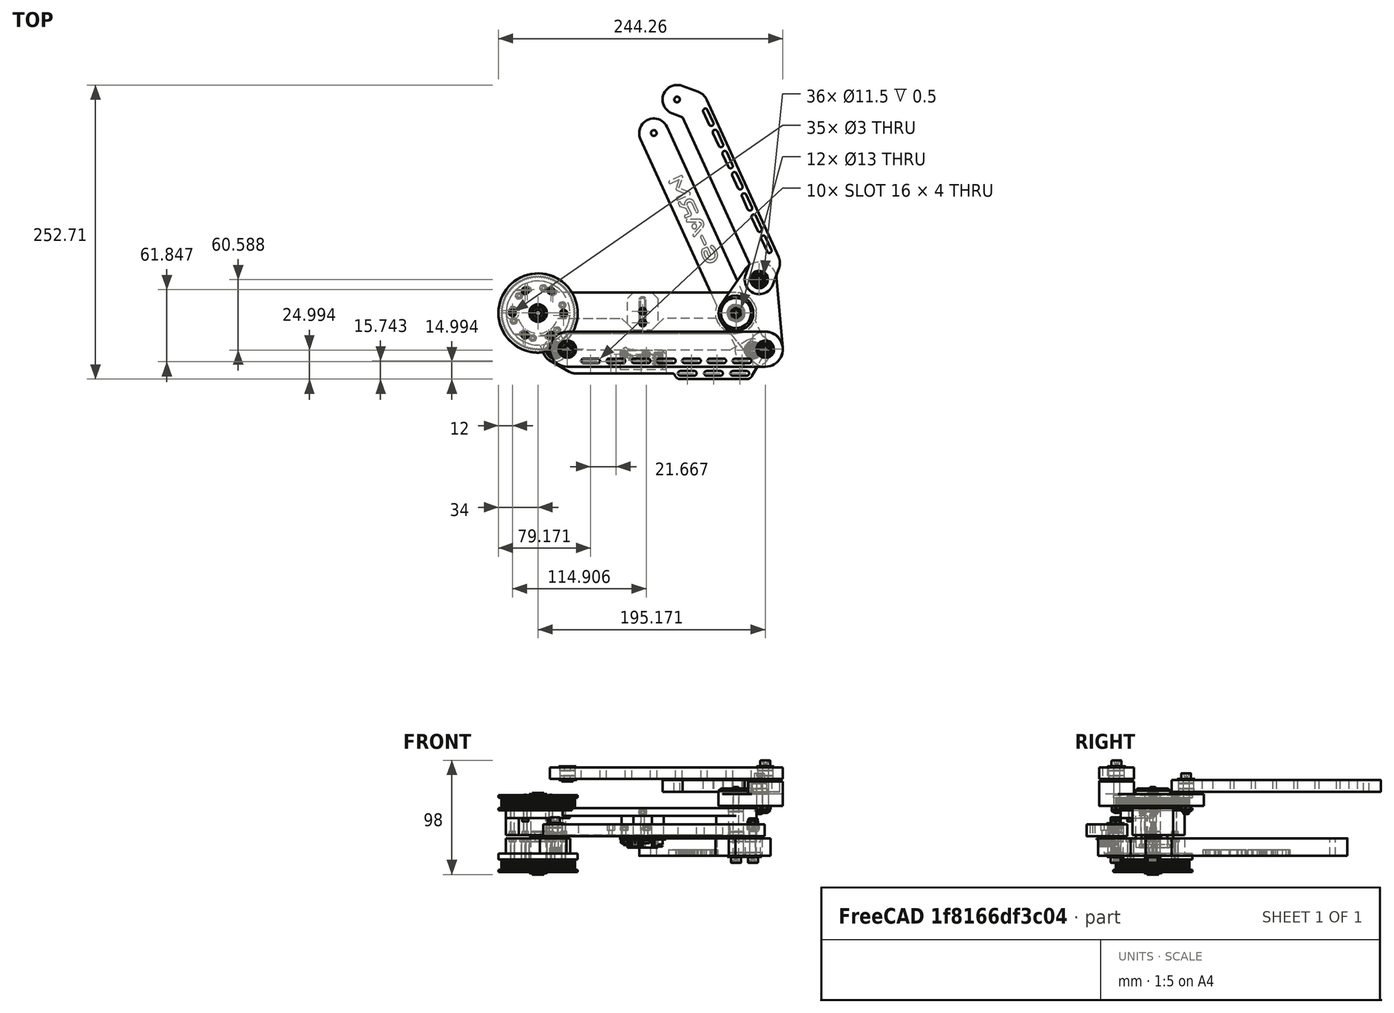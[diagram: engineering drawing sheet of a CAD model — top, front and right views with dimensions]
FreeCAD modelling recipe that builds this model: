
FCSTD DOCUMENT  (FreeCAD 0.20R29410 (Git))
Label: #0_ASSEMBLY_LINKS
License: All rights reserved
LicenseURL: http://en.wikipedia.org/wiki/All_rights_reserved
objects: Part::FeaturePython×105, App::FeaturePython×86
note: 105 computed .brp shape members not serialized (recipe doc carries the construction recipe); baked Part::Feature solids carry a one-line shape summary decoded from their .brp

FEATURE [Part::FeaturePython] b__11_Link1_001_  label="#11_Link1_001"  # a2plus imported part (geometry in sourceFile) (typed FeaturePython)
  a2p_Version = 0.4.60k
  fixedPosition = true
  objectType = a2pPart
  sourceFile = .\#11_Link1.FCStd
  subassemblyImport = false
  timeLastImport = 1.68867e+09
  updateColors = true
FEATURE [Part::FeaturePython] b_F6951_001_  label="F6951_001"  # a2plus imported part (geometry in sourceFile) (typed FeaturePython)
  Placement = pos=(-2.35677e-08,2.78792e-08,3) rot=(0.871292,0.490765,0;3.14159rad)
  a2p_Version = 0.4.60k
  fixedPosition = false
  objectType = a2pPart
  sourceFile = .\..\Complements\F695.step
  subassemblyImport = false
  timeLastImport = 1.6885e+09
  updateColors = true
FEATURE [Part::FeaturePython] b_F6951_001_001  label="F6951_002"  # a2plus imported part (geometry in sourceFile) (typed FeaturePython)
  Placement = pos=(170,-3.90484e-08,3) rot=(-0.661453,0.749987,0;3.14159rad)
  a2p_Version = 0.4.60k
  fixedPosition = false
  objectType = a2pPart
  sourceFile = .\..\Complements\F695.step
  subassemblyImport = false
  timeLastImport = 1.6885e+09
  updateColors = true
FEATURE [Part::FeaturePython] b_F6951_001_002  label="F6951_003"  # a2plus imported part (geometry in sourceFile) (typed FeaturePython)
  Placement = pos=(170,-4.90656e-08,20) rot=(-2e-06,0,1;0.008933rad)
  a2p_Version = 0.4.60k
  fixedPosition = false
  objectType = a2pPart
  sourceFile = .\..\Complements\F695.step
  subassemblyImport = false
  timeLastImport = 1.6885e+09
  updateColors = true
FEATURE [Part::FeaturePython] b_F6951_001_003  label="F6951_004"  # a2plus imported part (geometry in sourceFile) (typed FeaturePython)
  Placement = pos=(170,8.08089e-07,-6) rot=(1.8e-05,1.3e-05,-1;0.009624rad)
  a2p_Version = 0.4.60k
  fixedPosition = false
  objectType = a2pPart
  sourceFile = .\..\Complements\F695.step
  subassemblyImport = false
  timeLastImport = 1.6885e+09
  updateColors = true
FEATURE [Part::FeaturePython] b_F6951_001_005  label="F6951_006"  # a2plus imported part (geometry in sourceFile) (typed FeaturePython)
  Placement = pos=(0,1.12014e-07,31) rot=(0,0,1;0rad)
  a2p_Version = 0.4.60k
  fixedPosition = false
  objectType = a2pPart
  sourceFile = .\..\Complements\F695.step
  subassemblyImport = false
  timeLastImport = 1.6885e+09
  updateColors = true
FEATURE [Part::FeaturePython] b_F6951_001_006  label="F6951_007"  # a2plus imported part (geometry in sourceFile) (typed FeaturePython)
  Placement = pos=(184.542,-31.8361,-6.00001) rot=(0.000409,0.000277,1;0.00082rad)
  a2p_Version = 0.4.60k
  fixedPosition = false
  objectType = a2pPart
  sourceFile = .\..\Complements\F695.step
  subassemblyImport = false
  timeLastImport = 1.6885e+09
  updateColors = true
FEATURE [Part::FeaturePython] b_F6951_001_007  label="F6951_008"  # a2plus imported part (geometry in sourceFile) (typed FeaturePython)
  Placement = pos=(170,3.90411e-06,-15) rot=(-0.543177,0.839618,0;3.14159rad)
  a2p_Version = 0.4.60k
  fixedPosition = false
  objectType = a2pPart
  sourceFile = .\..\Complements\F695.step
  subassemblyImport = false
  timeLastImport = 1.6885e+09
  updateColors = true
FEATURE [Part::FeaturePython] b_F6951_001_008  label="F6951_009"  # a2plus imported part (geometry in sourceFile) (typed FeaturePython)
  Placement = pos=(1.64685e-07,-6.27281e-08,-6) rot=(0,-1e-06,-1;0.041178rad)
  a2p_Version = 0.4.60k
  fixedPosition = false
  objectType = a2pPart
  sourceFile = .\..\Complements\F695.step
  subassemblyImport = false
  timeLastImport = 1.6885e+09
  updateColors = true
FEATURE [Part::FeaturePython] b_F6951_001_009  label="F6951_010"  # a2plus imported part (geometry in sourceFile) (typed FeaturePython)
  Placement = pos=(184.542,-31.8361,-15) rot=(0.590696,0.806894,0;3.14159rad)
  a2p_Version = 0.4.60k
  fixedPosition = false
  objectType = a2pPart
  sourceFile = .\..\Complements\F695.step
  subassemblyImport = false
  timeLastImport = 1.6885e+09
  updateColors = true
FEATURE [App::FeaturePython] circularEdge_001  label="circularEdge_001__#11_Link1_001"  # a2plus constraint (typed FeaturePython)
  Object1 = b_F6951_001_
  Object2 = b__11_Link1_001_
  ParentTreeObject = -> b_F6951_001_
  SubElement1 = Edge18
  SubElement2 = Edge14
  Suppressed = false
  Type = circularEdge
  directionConstraint = 1
  lockRotation = false
  offset = 0
FEATURE [App::FeaturePython] circularEdge_001_mirror  label="circularEdge_001__F6951_001"  # a2plus constraint (typed FeaturePython)
  Object1 = b_F6951_001_
  Object2 = b__11_Link1_001_
  ParentTreeObject = -> b__11_Link1_001_
  SubElement1 = Edge18
  SubElement2 = Edge14
  Suppressed = false
  Type = circularEdge
  directionConstraint = 1
  lockRotation = false
  offset = 0
FEATURE [App::FeaturePython] circularEdge_002  label="circularEdge_002__#11_Link1_001"  # a2plus constraint (typed FeaturePython)
  Object1 = b_F6951_001_001
  Object2 = b__11_Link1_001_
  ParentTreeObject = -> b_F6951_001_001
  SubElement1 = Edge18
  SubElement2 = Edge18
  Suppressed = false
  Type = circularEdge
  directionConstraint = 1
  lockRotation = false
  offset = 0
FEATURE [App::FeaturePython] circularEdge_002_mirror  label="circularEdge_002__F6951_002"  # a2plus constraint (typed FeaturePython)
  Object1 = b_F6951_001_001
  Object2 = b__11_Link1_001_
  ParentTreeObject = -> b__11_Link1_001_
  SubElement1 = Edge18
  SubElement2 = Edge18
  Suppressed = false
  Type = circularEdge
  directionConstraint = 1
  lockRotation = false
  offset = 0
FEATURE [App::FeaturePython] circularEdge_003  label="circularEdge_003__#11_Link1_001"  # a2plus constraint (typed FeaturePython)
  Object1 = b_F6951_001_002
  Object2 = b__11_Link1_001_
  ParentTreeObject = -> b_F6951_001_002
  SubElement1 = Edge18
  SubElement2 = Edge62
  Suppressed = false
  Type = circularEdge
  directionConstraint = 0
  lockRotation = false
  offset = 0
FEATURE [App::FeaturePython] circularEdge_003_mirror  label="circularEdge_003__F6951_003"  # a2plus constraint (typed FeaturePython)
  Object1 = b_F6951_001_002
  Object2 = b__11_Link1_001_
  ParentTreeObject = -> b__11_Link1_001_
  SubElement1 = Edge18
  SubElement2 = Edge62
  Suppressed = false
  Type = circularEdge
  directionConstraint = 0
  lockRotation = false
  offset = 0
FEATURE [Part::FeaturePython] b__10_MotorsBasePulleys_001_  label="#10_MotorsBasePulleys_001"  # a2plus imported part (geometry in sourceFile) (typed FeaturePython)
  Placement = pos=(-11.651,-43.4819,23) rot=(0,0,1;0.523599rad)
  a2p_Version = 0.4.60k
  fixedPosition = false
  objectType = a2pPart
  sourceFile = .\#10_MotorsBasePulleys.FCStd
  subassemblyImport = false
  timeLastImport = 1.68295e+09
  updateColors = true
FEATURE [App::FeaturePython] circularEdge_004  label="circularEdge_004__#11_Link1_001"  # a2plus constraint (typed FeaturePython)
  Object1 = b__10_MotorsBasePulleys_001_
  Object2 = b__11_Link1_001_
  ParentTreeObject = -> b__10_MotorsBasePulleys_001_
  SubElement1 = Edge2166
  SubElement2 = Edge47
  Suppressed = false
  Type = circularEdge
  directionConstraint = 0
  lockRotation = false
  offset = 0
FEATURE [App::FeaturePython] circularEdge_004_mirror  label="circularEdge_004__#10_MotorsBasePulleys_001"  # a2plus constraint (typed FeaturePython)
  Object1 = b__10_MotorsBasePulleys_001_
  Object2 = b__11_Link1_001_
  ParentTreeObject = -> b__11_Link1_001_
  SubElement1 = Edge2166
  SubElement2 = Edge47
  Suppressed = false
  Type = circularEdge
  directionConstraint = 0
  lockRotation = false
  offset = 0
FEATURE [App::FeaturePython] circularEdge_005  label="circularEdge_005__#10_MotorsBasePulleys_001"  # a2plus constraint (typed FeaturePython)
  Object1 = b_F6951_001_005
  Object2 = b__10_MotorsBasePulleys_001_
  ParentTreeObject = -> b_F6951_001_005
  SubElement1 = Edge18
  SubElement2 = Edge716
  Suppressed = false
  Type = circularEdge
  directionConstraint = 0
  lockRotation = false
  offset = 0
FEATURE [App::FeaturePython] circularEdge_005_mirror  label="circularEdge_005__F6951_006"  # a2plus constraint (typed FeaturePython)
  Object1 = b_F6951_001_005
  Object2 = b__10_MotorsBasePulleys_001_
  ParentTreeObject = -> b__10_MotorsBasePulleys_001_
  SubElement1 = Edge18
  SubElement2 = Edge716
  Suppressed = false
  Type = circularEdge
  directionConstraint = 0
  lockRotation = false
  offset = 0
FEATURE [Part::FeaturePython] Screw  label="M3x30-Tornillo"  # Fasteners workbench fastener (typed FeaturePython)
  Placement = pos=(-22,0,3) rot=(1,0,0;3.14159rad)
  baseObject = -> b__11_Link1_001_ [Edge85]
  diameter = 4
  invert = false
  leftHanded = false
  length = 10
  lengthCustom = 30
  matchOuter = false
  offset = 0
  thread = false
  type = 45
FEATURE [Part::FeaturePython] Screw001  label="M3x30-Tornillo001"  # Fasteners workbench fastener (typed FeaturePython)
  Placement = pos=(22,-3e-15,3) rot=(1,0,0;3.14159rad)
  baseObject = -> b__11_Link1_001_ [Edge87]
  diameter = 4
  invert = false
  leftHanded = false
  length = 10
  lengthCustom = 30
  matchOuter = false
  offset = 0
  thread = false
  type = 45
FEATURE [Part::FeaturePython] Screw002  label="M3x30-Tornillo002"  # Fasteners workbench fastener (typed FeaturePython)
  Placement = pos=(11,19.0526,3) rot=(1,0,0;3.14159rad)
  baseObject = -> b__11_Link1_001_ [Edge103]
  diameter = 4
  invert = false
  leftHanded = false
  length = 10
  lengthCustom = 30
  matchOuter = false
  offset = 0
  thread = false
  type = 45
FEATURE [Part::FeaturePython] Screw003  label="M3x30-Tornillo003"  # Fasteners workbench fastener (typed FeaturePython)
  Placement = pos=(-11,19.0526,3) rot=(1,0,0;3.14159rad)
  baseObject = -> b__11_Link1_001_ [Edge101]
  diameter = 4
  invert = false
  leftHanded = false
  length = 10
  lengthCustom = 30
  matchOuter = false
  offset = 0
  thread = false
  type = 45
FEATURE [App::FeaturePython] circularEdge_006  label="circularEdge_006__#11_Link1_001"  # a2plus constraint (typed FeaturePython)
  Object1 = b__10_MotorsBasePulleys_001_
  Object2 = b__11_Link1_001_
  ParentTreeObject = -> b__10_MotorsBasePulleys_001_
  SubElement1 = Edge2217
  SubElement2 = Edge55
  Suppressed = false
  Type = circularEdge
  directionConstraint = 1
  lockRotation = false
  offset = 0
FEATURE [App::FeaturePython] circularEdge_006_mirror  label="circularEdge_006__#10_MotorsBasePulleys_001"  # a2plus constraint (typed FeaturePython)
  Object1 = b__10_MotorsBasePulleys_001_
  Object2 = b__11_Link1_001_
  ParentTreeObject = -> b__11_Link1_001_
  SubElement1 = Edge2217
  SubElement2 = Edge55
  Suppressed = false
  Type = circularEdge
  directionConstraint = 1
  lockRotation = false
  offset = 0
FEATURE [Part::FeaturePython] Screw004  label="M3x20-Tornillo"  # Fasteners workbench fastener (typed FeaturePython)
  Placement = pos=(-11,-19.0526,14.5) rot=(1,0,0;3.14159rad)
  baseObject = -> b__11_Link1_001_ [Edge123]
  diameter = 4
  invert = false
  leftHanded = false
  length = 10
  lengthCustom = 20
  matchOuter = false
  offset = 0
  thread = false
  type = 45
FEATURE [Part::FeaturePython] Screw005  label="M3x20-Tornillo001"  # Fasteners workbench fastener (typed FeaturePython)
  Placement = pos=(11,-19.0526,14.5) rot=(1,0,0;3.14159rad)
  baseObject = -> b__11_Link1_001_ [Edge121]
  diameter = 4
  invert = false
  leftHanded = false
  length = 10
  lengthCustom = 20
  matchOuter = false
  offset = 0
  thread = false
  type = 45
FEATURE [Part::FeaturePython] Nut  label="M3-Tuerca"  # Fasteners workbench fastener (typed FeaturePython)
  Placement = pos=(-22,7.42124e-07,29) rot=(0,0,1;0rad)
  baseObject = -> b__10_MotorsBasePulleys_001_ [Edge2224]
  diameter = 1
  invert = false
  leftHanded = false
  matchOuter = false
  offset = 0
  thread = false
  type = 19
FEATURE [Part::FeaturePython] Nut001  label="M3-Tuerca001"  # Fasteners workbench fastener (typed FeaturePython)
  Placement = pos=(-11,19.0526,29) rot=(0,0,1;0rad)
  baseObject = -> b__10_MotorsBasePulleys_001_ [Edge2226]
  diameter = 1
  invert = false
  leftHanded = false
  matchOuter = false
  offset = 0
  thread = false
  type = 19
FEATURE [Part::FeaturePython] Nut002  label="M3-Tuerca002"  # Fasteners workbench fastener (typed FeaturePython)
  Placement = pos=(11,19.0526,29) rot=(0,0,1;0rad)
  baseObject = -> b__10_MotorsBasePulleys_001_ [Edge2225]
  diameter = 1
  invert = false
  leftHanded = false
  matchOuter = false
  offset = 0
  thread = false
  type = 19
FEATURE [Part::FeaturePython] Nut003  label="M3-Tuerca003"  # Fasteners workbench fastener (typed FeaturePython)
  Placement = pos=(-11,-19.0526,29) rot=(0,0,1;0rad)
  baseObject = -> b__10_MotorsBasePulleys_001_ [Edge2222]
  diameter = 1
  invert = false
  leftHanded = false
  matchOuter = false
  offset = 0
  thread = false
  type = 19
FEATURE [Part::FeaturePython] Nut004  label="M3-Tuerca004"  # Fasteners workbench fastener (typed FeaturePython)
  Placement = pos=(22,-2.47375e-07,29) rot=(0,0,1;0rad)
  baseObject = -> b__10_MotorsBasePulleys_001_ [Edge2223]
  diameter = 1
  invert = false
  leftHanded = false
  matchOuter = false
  offset = 0
  thread = false
  type = 19
FEATURE [Part::FeaturePython] Nut005  label="M3-Tuerca005"  # Fasteners workbench fastener (typed FeaturePython)
  Placement = pos=(11,-19.0526,29) rot=(0,0,1;0rad)
  baseObject = -> b__10_MotorsBasePulleys_001_ [Edge2221]
  diameter = 1
  invert = false
  leftHanded = false
  matchOuter = false
  offset = 0
  thread = false
  type = 19
FEATURE [Part::FeaturePython] Nut006  label="M3-Tuerca008"  # Fasteners workbench fastener (typed FeaturePython)
  Placement = pos=(89.762,1.5,18) rot=(0,0,1;0rad)
  baseObject = -> b__11_Link1_001_ [Edge79]
  diameter = 1
  invert = true
  leftHanded = false
  matchOuter = false
  offset = 0
  thread = false
  type = 19
FEATURE [Part::FeaturePython] Nut007  label="M3-Tuerca009"  # Fasteners workbench fastener (typed FeaturePython)
  Placement = pos=(89.762,-8.5,18) rot=(0,0,1;0rad)
  baseObject = -> b__11_Link1_001_ [Edge77]
  diameter = 1
  invert = true
  leftHanded = false
  matchOuter = false
  offset = 0
  thread = false
  type = 19
FEATURE [Part::FeaturePython] b__18_EndStopLink2Adjust_001_  label="#18_EndStopLink2Adjust_001"  # a2plus imported part (geometry in sourceFile) (typed FeaturePython)
  Placement = pos=(89.762,1.5,-9.71845e-08) rot=(-0.707107,0.707107,0;3.14159rad)
  a2p_Version = 0.4.60k
  fixedPosition = false
  objectType = a2pPart
  sourceFile = .\#18_EndStopLink2Adjust.FCStd
  subassemblyImport = false
  timeLastImport = 1.68302e+09
  updateColors = true
FEATURE [App::FeaturePython] angledPlanes_001  label="angledPlanes_001__#11_Link1_001"  # a2plus constraint (typed FeaturePython)
  Object1 = b__18_EndStopLink2Adjust_001_
  Object2 = b__11_Link1_001_
  ParentTreeObject = -> b__18_EndStopLink2Adjust_001_
  SubElement1 = Face14
  SubElement2 = Face9
  Suppressed = false
  Type = angledPlanes
  angle = 90
FEATURE [App::FeaturePython] angledPlanes_001_mirror  label="angledPlanes_001__#18_EndStopLink2Adjust_001"  # a2plus constraint (typed FeaturePython)
  Object1 = b__18_EndStopLink2Adjust_001_
  Object2 = b__11_Link1_001_
  ParentTreeObject = -> b__11_Link1_001_
  SubElement1 = Face14
  SubElement2 = Face9
  Suppressed = false
  Type = angledPlanes
  angle = 90
FEATURE [Part::FeaturePython] Screw006  label="M3x30-Tornillo006"  # Fasteners workbench fastener (typed FeaturePython)
  Placement = pos=(89.762,-8.5,-8) rot=(1,0,0;3.14159rad)
  baseObject = -> b__11_Link1_001_ [Edge16]
  diameter = 4
  invert = false
  leftHanded = false
  length = 10
  lengthCustom = 30
  matchOuter = false
  offset = 8
  thread = false
  type = 45
FEATURE [Part::FeaturePython] Screw007  label="M3x30-Tornillo005"  # Fasteners workbench fastener (typed FeaturePython)
  Placement = pos=(89.762,1.5,-8) rot=(1,0,0;3.14159rad)
  baseObject = -> b__11_Link1_001_ [Edge17]
  diameter = 4
  invert = false
  leftHanded = false
  length = 10
  lengthCustom = 30
  matchOuter = false
  offset = 8
  thread = false
  type = 45
FEATURE [Part::FeaturePython] Washer  label="M5-Arandela"  # Fasteners workbench fastener (typed FeaturePython)
  Placement = pos=(-7.78767e-09,1.38263e-08,-1) rot=(0.871295,0.490759,0;3.14159rad)
  baseObject = -> b_F6951_001_ [Edge17]
  diameter = 6
  invert = true
  matchOuter = false
  offset = 0
  type = 4
FEATURE [Part::FeaturePython] M5_Arandela_001  label="M5-Arandela_001"  # a2plus imported part (geometry in sourceFile) (typed FeaturePython)
  Placement = pos=(3.60617e-08,-3.8045e-08,-3) rot=(0.871295,0.490759,0;3.14159rad)
  a2p_Version = 0.4.60k
  fixedPosition = false
  localSourceObject = Washer
  objectType = a2pPart
  sourceFile = converted
  subassemblyImport = false
  timeLastImport = 1.689e+09
  updateColors = true
FEATURE [App::FeaturePython] circularEdge_008  label="circularEdge_008__F6951_001"  # a2plus constraint (typed FeaturePython)
  Object1 = M5_Arandela_001
  Object2 = b_F6951_001_
  ParentTreeObject = -> M5_Arandela_001
  SubElement1 = Edge2
  SubElement2 = Edge8
  Suppressed = false
  Type = circularEdge
  directionConstraint = 1
  lockRotation = false
  offset = 0
FEATURE [App::FeaturePython] circularEdge_008_mirror  label="circularEdge_008__M5-Arandela_001"  # a2plus constraint (typed FeaturePython)
  Object1 = M5_Arandela_001
  Object2 = b_F6951_001_
  ParentTreeObject = -> b_F6951_001_
  SubElement1 = Edge2
  SubElement2 = Edge8
  Suppressed = false
  Type = circularEdge
  directionConstraint = 1
  lockRotation = false
  offset = 0
FEATURE [Part::FeaturePython] b_M5_Arandela_001_  label="M5-Arandela_002"  # a2plus imported part (geometry in sourceFile) (typed FeaturePython)
  Placement = pos=(170,1.78434e-07,-3) rot=(0.874462,0.485093,0;3.14159rad)
  a2p_Version = 0.4.60k
  fixedPosition = false
  localSourceObject = Washer
  objectType = a2pPart
  sourceFile = converted
  subassemblyImport = false
  timeLastImport = 1.689e+09
  updateColors = true
FEATURE [Part::FeaturePython] b_M5_Arandela_001_001  label="M5-Arandela_003"  # a2plus imported part (geometry in sourceFile) (typed FeaturePython)
  Placement = pos=(184.542,-31.8361,-3.00001) rot=(0.872092,0.489343,0;3.14159rad)
  a2p_Version = 0.4.60k
  fixedPosition = false
  localSourceObject = Washer
  objectType = a2pPart
  sourceFile = converted
  subassemblyImport = false
  timeLastImport = 1.689e+09
  updateColors = true
FEATURE [Part::FeaturePython] b_M5_Arandela_001_002  label="M5-Arandela_004"  # a2plus imported part (geometry in sourceFile) (typed FeaturePython)
  Placement = pos=(14.5419,-31.8361,-4) rot=(0.876459,0.481477,0;3.14159rad)
  a2p_Version = 0.4.60k
  fixedPosition = false
  localSourceObject = Washer
  objectType = a2pPart
  sourceFile = converted
  subassemblyImport = false
  timeLastImport = 1.689e+09
  updateColors = true
FEATURE [App::FeaturePython] circularEdge_009  label="circularEdge_009__F6951_002"  # a2plus constraint (typed FeaturePython)
  Object1 = b_M5_Arandela_001_
  Object2 = b_F6951_001_001
  ParentTreeObject = -> b_M5_Arandela_001_
  SubElement1 = Edge2
  SubElement2 = Edge14
  Suppressed = false
  Type = circularEdge
  directionConstraint = 1
  lockRotation = false
  offset = 0
FEATURE [App::FeaturePython] circularEdge_009_mirror  label="circularEdge_009__M5-Arandela_002"  # a2plus constraint (typed FeaturePython)
  Object1 = b_M5_Arandela_001_
  Object2 = b_F6951_001_001
  ParentTreeObject = -> b_F6951_001_001
  SubElement1 = Edge2
  SubElement2 = Edge14
  Suppressed = false
  Type = circularEdge
  directionConstraint = 1
  lockRotation = false
  offset = 0
FEATURE [App::FeaturePython] circularEdge_010  label="circularEdge_010__M5-Arandela_002"  # a2plus constraint (typed FeaturePython)
  Object1 = b_F6951_001_003
  Object2 = b_M5_Arandela_001_
  ParentTreeObject = -> b_F6951_001_003
  SubElement1 = Edge14
  SubElement2 = Edge3
  Suppressed = false
  Type = circularEdge
  directionConstraint = 0
  lockRotation = false
  offset = 0
FEATURE [App::FeaturePython] circularEdge_010_mirror  label="circularEdge_010__F6951_004"  # a2plus constraint (typed FeaturePython)
  Object1 = b_F6951_001_003
  Object2 = b_M5_Arandela_001_
  ParentTreeObject = -> b_M5_Arandela_001_
  SubElement1 = Edge14
  SubElement2 = Edge3
  Suppressed = false
  Type = circularEdge
  directionConstraint = 0
  lockRotation = false
  offset = 0
FEATURE [Part::FeaturePython] b__19_Link2_001_  label="#19_Link2_001"  # a2plus imported part (geometry in sourceFile) (typed FeaturePython)
  Placement = pos=(170,2.89051e-07,-3) rot=(0.54061,0.841273,0;3.14159rad)
  a2p_Version = 0.4.60k
  fixedPosition = false
  objectType = a2pPart
  sourceFile = .\#19_Link2.FCStd
  subassemblyImport = false
  timeLastImport = 1.68302e+09
  updateColors = true
FEATURE [App::FeaturePython] circularEdge_011  label="circularEdge_011__F6951_004"  # a2plus constraint (typed FeaturePython)
  Object1 = b__19_Link2_001_
  Object2 = b_F6951_001_003
  ParentTreeObject = -> b__19_Link2_001_
  SubElement1 = Edge17
  SubElement2 = Edge18
  Suppressed = false
  Type = circularEdge
  directionConstraint = 1
  lockRotation = false
  offset = 0
FEATURE [App::FeaturePython] circularEdge_011_mirror  label="circularEdge_011__#19_Link2_001"  # a2plus constraint (typed FeaturePython)
  Object1 = b__19_Link2_001_
  Object2 = b_F6951_001_003
  ParentTreeObject = -> b_F6951_001_003
  SubElement1 = Edge17
  SubElement2 = Edge18
  Suppressed = false
  Type = circularEdge
  directionConstraint = 1
  lockRotation = false
  offset = 0
FEATURE [App::FeaturePython] circularEdge_012  label="circularEdge_012__#19_Link2_001"  # a2plus constraint (typed FeaturePython)
  Object1 = b_F6951_001_007
  Object2 = b__19_Link2_001_
  ParentTreeObject = -> b_F6951_001_007
  SubElement1 = Edge18
  SubElement2 = Edge25
  Suppressed = false
  Type = circularEdge
  directionConstraint = 0
  lockRotation = false
  offset = 0
FEATURE [App::FeaturePython] circularEdge_012_mirror  label="circularEdge_012__F6951_008"  # a2plus constraint (typed FeaturePython)
  Object1 = b_F6951_001_007
  Object2 = b__19_Link2_001_
  ParentTreeObject = -> b__19_Link2_001_
  SubElement1 = Edge18
  SubElement2 = Edge25
  Suppressed = false
  Type = circularEdge
  directionConstraint = 0
  lockRotation = false
  offset = 0
FEATURE [App::FeaturePython] circularEdge_013  label="circularEdge_013__#19_Link2_001"  # a2plus constraint (typed FeaturePython)
  Object1 = b_F6951_001_009
  Object2 = b__19_Link2_001_
  ParentTreeObject = -> b_F6951_001_009
  SubElement1 = Edge18
  SubElement2 = Edge24
  Suppressed = false
  Type = circularEdge
  directionConstraint = 0
  lockRotation = false
  offset = 0
FEATURE [App::FeaturePython] circularEdge_013_mirror  label="circularEdge_013__F6951_010"  # a2plus constraint (typed FeaturePython)
  Object1 = b_F6951_001_009
  Object2 = b__19_Link2_001_
  ParentTreeObject = -> b__19_Link2_001_
  SubElement1 = Edge18
  SubElement2 = Edge24
  Suppressed = false
  Type = circularEdge
  directionConstraint = 0
  lockRotation = false
  offset = 0
FEATURE [App::FeaturePython] circularEdge_014  label="circularEdge_014__#19_Link2_001"  # a2plus constraint (typed FeaturePython)
  Object1 = b_F6951_001_006
  Object2 = b__19_Link2_001_
  ParentTreeObject = -> b_F6951_001_006
  SubElement1 = Edge18
  SubElement2 = Edge16
  Suppressed = false
  Type = circularEdge
  directionConstraint = 1
  lockRotation = false
  offset = 0
FEATURE [App::FeaturePython] circularEdge_014_mirror  label="circularEdge_014__F6951_007"  # a2plus constraint (typed FeaturePython)
  Object1 = b_F6951_001_006
  Object2 = b__19_Link2_001_
  ParentTreeObject = -> b__19_Link2_001_
  SubElement1 = Edge18
  SubElement2 = Edge16
  Suppressed = false
  Type = circularEdge
  directionConstraint = 1
  lockRotation = false
  offset = 0
FEATURE [App::FeaturePython] circularEdge_015  label="circularEdge_015__F6951_007"  # a2plus constraint (typed FeaturePython)
  Object1 = b_M5_Arandela_001_001
  Object2 = b_F6951_001_006
  ParentTreeObject = -> b_M5_Arandela_001_001
  SubElement1 = Edge3
  SubElement2 = Edge8
  Suppressed = false
  Type = circularEdge
  directionConstraint = 0
  lockRotation = false
  offset = 0
FEATURE [App::FeaturePython] circularEdge_015_mirror  label="circularEdge_015__M5-Arandela_003"  # a2plus constraint (typed FeaturePython)
  Object1 = b_M5_Arandela_001_001
  Object2 = b_F6951_001_006
  ParentTreeObject = -> b_F6951_001_006
  SubElement1 = Edge3
  SubElement2 = Edge8
  Suppressed = false
  Type = circularEdge
  directionConstraint = 0
  lockRotation = false
  offset = 0
FEATURE [Part::FeaturePython] b__14_Joint2Crank_001_  label="#14_Joint2Crank_001"  # a2plus imported part (geometry in sourceFile) (typed FeaturePython)
  Placement = pos=(7.98786e-07,-1.2555e-07,-16) rot=(0,0,-1;1.14232rad)
  a2p_Version = 0.4.60k
  fixedPosition = false
  objectType = a2pPart
  sourceFile = .\#14_Joint2Crank.FCStd
  subassemblyImport = false
  timeLastImport = 1.68301e+09
  updateColors = true
FEATURE [App::FeaturePython] circularEdge_017  label="circularEdge_017__M5-Arandela_001"  # a2plus constraint (typed FeaturePython)
  Object1 = b_F6951_001_008
  Object2 = M5_Arandela_001
  ParentTreeObject = -> b_F6951_001_008
  SubElement1 = Edge14
  SubElement2 = Edge3
  Suppressed = false
  Type = circularEdge
  directionConstraint = 0
  lockRotation = false
  offset = 0
FEATURE [App::FeaturePython] circularEdge_017_mirror  label="circularEdge_017__F6951_009"  # a2plus constraint (typed FeaturePython)
  Object1 = b_F6951_001_008
  Object2 = M5_Arandela_001
  ParentTreeObject = -> M5_Arandela_001
  SubElement1 = Edge14
  SubElement2 = Edge3
  Suppressed = false
  Type = circularEdge
  directionConstraint = 0
  lockRotation = false
  offset = 0
FEATURE [App::FeaturePython] circularEdge_018  label="circularEdge_018__F6951_009"  # a2plus constraint (typed FeaturePython)
  Object1 = b__14_Joint2Crank_001_
  Object2 = b_F6951_001_008
  ParentTreeObject = -> b__14_Joint2Crank_001_
  SubElement1 = Edge29
  SubElement2 = Edge18
  Suppressed = false
  Type = circularEdge
  directionConstraint = 0
  lockRotation = false
  offset = 0
FEATURE [App::FeaturePython] circularEdge_018_mirror  label="circularEdge_018__#14_Joint2Crank_001"  # a2plus constraint (typed FeaturePython)
  Object1 = b__14_Joint2Crank_001_
  Object2 = b_F6951_001_008
  ParentTreeObject = -> b_F6951_001_008
  SubElement1 = Edge29
  SubElement2 = Edge18
  Suppressed = false
  Type = circularEdge
  directionConstraint = 0
  lockRotation = false
  offset = 0
FEATURE [Part::FeaturePython] b_F6951_001_010  label="F6951_011"  # a2plus imported part (geometry in sourceFile) (typed FeaturePython)
  Placement = pos=(1.33186e-06,-8.25365e-07,-29) rot=(0.812104,0.583513,0;3.14159rad)
  a2p_Version = 0.4.60k
  fixedPosition = false
  objectType = a2pPart
  sourceFile = .\..\Complements\F695.step
  subassemblyImport = false
  timeLastImport = 1.6885e+09
  updateColors = true
FEATURE [Part::FeaturePython] b_F6951_001_011  label="F6951_012"  # a2plus imported part (geometry in sourceFile) (typed FeaturePython)
  Placement = pos=(14.5419,-31.8361,2) rot=(0.891544,-0.452934,0;3.14159rad)
  a2p_Version = 0.4.60k
  fixedPosition = false
  objectType = a2pPart
  sourceFile = .\..\Complements\F695.step
  subassemblyImport = false
  timeLastImport = 1.6885e+09
  updateColors = true
FEATURE [App::FeaturePython] circularEdge_022  label="circularEdge_022__#14_Joint2Crank_001"  # a2plus constraint (typed FeaturePython)
  Object1 = b_M5_Arandela_001_002
  Object2 = b__14_Joint2Crank_001_
  ParentTreeObject = -> b_M5_Arandela_001_002
  SubElement1 = Edge3
  SubElement2 = Edge32
  Suppressed = false
  Type = circularEdge
  directionConstraint = 0
  lockRotation = false
  offset = 0
FEATURE [App::FeaturePython] circularEdge_022_mirror  label="circularEdge_022__M5-Arandela_004"  # a2plus constraint (typed FeaturePython)
  Object1 = b_M5_Arandela_001_002
  Object2 = b__14_Joint2Crank_001_
  ParentTreeObject = -> b__14_Joint2Crank_001_
  SubElement1 = Edge3
  SubElement2 = Edge32
  Suppressed = false
  Type = circularEdge
  directionConstraint = 0
  lockRotation = false
  offset = 0
FEATURE [App::FeaturePython] circularEdge_023  label="circularEdge_023__M5-Arandela_004"  # a2plus constraint (typed FeaturePython)
  Object1 = b_F6951_001_011
  Object2 = b_M5_Arandela_001_002
  ParentTreeObject = -> b_F6951_001_011
  SubElement1 = Edge17
  SubElement2 = Edge1
  Suppressed = false
  Type = circularEdge
  directionConstraint = 0
  lockRotation = false
  offset = 0
FEATURE [App::FeaturePython] circularEdge_023_mirror  label="circularEdge_023__F6951_012"  # a2plus constraint (typed FeaturePython)
  Object1 = b_F6951_001_011
  Object2 = b_M5_Arandela_001_002
  ParentTreeObject = -> b_M5_Arandela_001_002
  SubElement1 = Edge17
  SubElement2 = Edge1
  Suppressed = false
  Type = circularEdge
  directionConstraint = 0
  lockRotation = false
  offset = 0
FEATURE [App::FeaturePython] circularEdge_007  label="circularEdge_007__#11_Link1_001"  # a2plus constraint (typed FeaturePython)
  Object1 = b__18_EndStopLink2Adjust_001_
  Object2 = b__11_Link1_001_
  ParentTreeObject = -> b__18_EndStopLink2Adjust_001_
  SubElement1 = Edge14
  SubElement2 = Edge16
  Suppressed = false
  Type = circularEdge
  directionConstraint = 0
  lockRotation = false
  offset = 0
FEATURE [App::FeaturePython] circularEdge_007_mirror  label="circularEdge_007__#18_EndStopLink2Adjust_001"  # a2plus constraint (typed FeaturePython)
  Object1 = b__18_EndStopLink2Adjust_001_
  Object2 = b__11_Link1_001_
  ParentTreeObject = -> b__11_Link1_001_
  SubElement1 = Edge14
  SubElement2 = Edge16
  Suppressed = false
  Type = circularEdge
  directionConstraint = 0
  lockRotation = false
  offset = 0
FEATURE [Part::FeaturePython] b__13_MotorsBasePulleyAntiSlip_001_  label="#13_MotorsBasePulleyAntiSlip_001"  # a2plus imported part (geometry in sourceFile) (typed FeaturePython)
  Placement = pos=(1.02348e-06,-2.14473e-07,-21) rot=(0,0,-1;0.618725rad)
  a2p_Version = 0.4.60k
  fixedPosition = false
  objectType = a2pPart
  sourceFile = .\#13_MotorsBasePulleyAntiSlip.FCStd
  subassemblyImport = false
  timeLastImport = 1.68301e+09
  updateColors = true
FEATURE [App::FeaturePython] circularEdge_019  label="circularEdge_019__#14_Joint2Crank_001"  # a2plus constraint (typed FeaturePython)
  Object1 = b__13_MotorsBasePulleyAntiSlip_001_
  Object2 = b__14_Joint2Crank_001_
  ParentTreeObject = -> b__13_MotorsBasePulleyAntiSlip_001_
  SubElement1 = Edge15
  SubElement2 = Edge21
  Suppressed = false
  Type = circularEdge
  directionConstraint = 0
  lockRotation = false
  offset = 0
FEATURE [App::FeaturePython] circularEdge_019_mirror  label="circularEdge_019__#13_MotorsBasePulleyAntiSlip_001"  # a2plus constraint (typed FeaturePython)
  Object1 = b__13_MotorsBasePulleyAntiSlip_001_
  Object2 = b__14_Joint2Crank_001_
  ParentTreeObject = -> b__14_Joint2Crank_001_
  SubElement1 = Edge15
  SubElement2 = Edge21
  Suppressed = false
  Type = circularEdge
  directionConstraint = 0
  lockRotation = false
  offset = 0
FEATURE [App::FeaturePython] circularEdge_024  label="circularEdge_024__#13_MotorsBasePulleyAntiSlip_001"  # a2plus constraint (typed FeaturePython)
  Object1 = b__14_Joint2Crank_001_
  Object2 = b__13_MotorsBasePulleyAntiSlip_001_
  ParentTreeObject = -> b__14_Joint2Crank_001_
  SubElement1 = Edge23
  SubElement2 = Edge13
  Suppressed = false
  Type = circularEdge
  directionConstraint = 0
  lockRotation = false
  offset = 0
FEATURE [App::FeaturePython] circularEdge_024_mirror  label="circularEdge_024__#14_Joint2Crank_001"  # a2plus constraint (typed FeaturePython)
  Object1 = b__14_Joint2Crank_001_
  Object2 = b__13_MotorsBasePulleyAntiSlip_001_
  ParentTreeObject = -> b__13_MotorsBasePulleyAntiSlip_001_
  SubElement1 = Edge23
  SubElement2 = Edge13
  Suppressed = false
  Type = circularEdge
  directionConstraint = 0
  lockRotation = false
  offset = 0
FEATURE [Part::FeaturePython] b__10_MotorsBasePulleys_001_001  label="#10_MotorsBasePulleys_002"  # a2plus imported part (geometry in sourceFile) (typed FeaturePython)
  Placement = pos=(-34.7105,-28.6637,-21) rot=(0.739927,0.672687,0;3.14159rad)
  a2p_Version = 0.4.60k
  fixedPosition = false
  objectType = a2pPart
  sourceFile = .\#10_MotorsBasePulleys.FCStd
  subassemblyImport = false
  timeLastImport = 1.68295e+09
  updateColors = true
FEATURE [App::FeaturePython] circularEdge_025  label="circularEdge_025__#13_MotorsBasePulleyAntiSlip_001"  # a2plus constraint (typed FeaturePython)
  Object1 = b__10_MotorsBasePulleys_001_001
  Object2 = b__13_MotorsBasePulleyAntiSlip_001_
  ParentTreeObject = -> b__10_MotorsBasePulleys_001_001
  SubElement1 = Edge2166
  SubElement2 = Edge8
  Suppressed = false
  Type = circularEdge
  directionConstraint = 1
  lockRotation = false
  offset = 0
FEATURE [App::FeaturePython] circularEdge_025_mirror  label="circularEdge_025__#10_MotorsBasePulleys_002"  # a2plus constraint (typed FeaturePython)
  Object1 = b__10_MotorsBasePulleys_001_001
  Object2 = b__13_MotorsBasePulleyAntiSlip_001_
  ParentTreeObject = -> b__13_MotorsBasePulleyAntiSlip_001_
  SubElement1 = Edge2166
  SubElement2 = Edge8
  Suppressed = false
  Type = circularEdge
  directionConstraint = 1
  lockRotation = false
  offset = 0
FEATURE [App::FeaturePython] circularEdge_026  label="circularEdge_026__#13_MotorsBasePulleyAntiSlip_001"  # a2plus constraint (typed FeaturePython)
  Object1 = b__10_MotorsBasePulleys_001_001
  Object2 = b__13_MotorsBasePulleyAntiSlip_001_
  ParentTreeObject = -> b__10_MotorsBasePulleys_001_001
  SubElement1 = Edge2220
  SubElement2 = Edge10
  Suppressed = false
  Type = circularEdge
  directionConstraint = 1
  lockRotation = false
  offset = 0
FEATURE [App::FeaturePython] circularEdge_026_mirror  label="circularEdge_026__#10_MotorsBasePulleys_002"  # a2plus constraint (typed FeaturePython)
  Object1 = b__10_MotorsBasePulleys_001_001
  Object2 = b__13_MotorsBasePulleyAntiSlip_001_
  ParentTreeObject = -> b__13_MotorsBasePulleyAntiSlip_001_
  SubElement1 = Edge2220
  SubElement2 = Edge10
  Suppressed = false
  Type = circularEdge
  directionConstraint = 1
  lockRotation = false
  offset = 0
FEATURE [Part::FeaturePython] Nut009  label="M3-Tuerca010"  # Fasteners workbench fastener (typed FeaturePython)
  Placement = pos=(20.9135,6.82822,-27) rot=(0.817934,0.575313,0;3.14159rad)
  baseObject = -> b__10_MotorsBasePulleys_001_001 [Edge2226]
  diameter = 1
  invert = false
  leftHanded = false
  matchOuter = false
  offset = 0
  thread = false
  type = 19
FEATURE [Part::FeaturePython] Nut010  label="M3-Tuerca011"  # Fasteners workbench fastener (typed FeaturePython)
  Placement = pos=(4.54335,21.5257,-27) rot=(0.817934,0.575313,0;3.14159rad)
  baseObject = -> b__10_MotorsBasePulleys_001_001 [Edge2225]
  diameter = 1
  invert = false
  leftHanded = false
  matchOuter = false
  offset = 0
  thread = false
  type = 19
FEATURE [Part::FeaturePython] Nut011  label="M3-Tuerca012"  # Fasteners workbench fastener (typed FeaturePython)
  Placement = pos=(-16.3702,14.6975,-27) rot=(0.817934,0.575313,0;3.14159rad)
  baseObject = -> b__10_MotorsBasePulleys_001_001 [Edge2223]
  diameter = 1
  invert = false
  leftHanded = false
  matchOuter = false
  offset = 0
  thread = false
  type = 19
FEATURE [Part::FeaturePython] Nut012  label="M3-Tuerca013"  # Fasteners workbench fastener (typed FeaturePython)
  Placement = pos=(-20.9135,-6.82822,-27) rot=(0.817934,0.575313,0;3.14159rad)
  baseObject = -> b__10_MotorsBasePulleys_001_001 [Edge2221]
  diameter = 1
  invert = false
  leftHanded = false
  matchOuter = false
  offset = 0
  thread = false
  type = 19
FEATURE [Part::FeaturePython] Nut013  label="M3-Tuerca014"  # Fasteners workbench fastener (typed FeaturePython)
  Placement = pos=(-4.54335,-21.5258,-27) rot=(0.817934,0.575313,0;3.14159rad)
  baseObject = -> b__10_MotorsBasePulleys_001_001 [Edge2222]
  diameter = 1
  invert = false
  leftHanded = false
  matchOuter = false
  offset = 0
  thread = false
  type = 19
FEATURE [Part::FeaturePython] Nut014  label="M3-Tuerca015"  # Fasteners workbench fastener (typed FeaturePython)
  Placement = pos=(16.3702,-14.6975,-27) rot=(0.817934,0.575313,0;3.14159rad)
  baseObject = -> b__10_MotorsBasePulleys_001_001 [Edge2224]
  diameter = 1
  invert = false
  leftHanded = false
  matchOuter = false
  offset = 0
  thread = false
  type = 19
FEATURE [App::FeaturePython] circularEdge_027  label="circularEdge_027__#10_MotorsBasePulleys_002"  # a2plus constraint (typed FeaturePython)
  Object1 = b_F6951_001_010
  Object2 = b__10_MotorsBasePulleys_001_001
  ParentTreeObject = -> b_F6951_001_010
  SubElement1 = Edge18
  SubElement2 = Edge716
  Suppressed = false
  Type = circularEdge
  directionConstraint = 0
  lockRotation = false
  offset = 0
FEATURE [App::FeaturePython] circularEdge_027_mirror  label="circularEdge_027__F6951_011"  # a2plus constraint (typed FeaturePython)
  Object1 = b_F6951_001_010
  Object2 = b__10_MotorsBasePulleys_001_001
  ParentTreeObject = -> b__10_MotorsBasePulleys_001_001
  SubElement1 = Edge18
  SubElement2 = Edge716
  Suppressed = false
  Type = circularEdge
  directionConstraint = 0
  lockRotation = false
  offset = 0
FEATURE [Part::FeaturePython] b_M5_Arandela_001_003  label="M5-Arandela_005"  # a2plus imported part (geometry in sourceFile) (typed FeaturePython)
  Placement = pos=(1.55146e-06,-1.54261e-06,-35) rot=(0.871295,0.490759,0;3.14159rad)
  a2p_Version = 0.4.60k
  fixedPosition = false
  localSourceObject = Washer
  objectType = a2pPart
  sourceFile = converted
  subassemblyImport = false
  timeLastImport = 1.689e+09
  updateColors = true
FEATURE [Part::FeaturePython] b_M5_Arandela_001_004  label="M5-Arandela_006"  # a2plus imported part (geometry in sourceFile) (typed FeaturePython)
  Placement = pos=(6.39923e-09,1.22067e-07,34) rot=(0.871295,0.490759,0;3.14159rad)
  a2p_Version = 0.4.60k
  fixedPosition = false
  localSourceObject = Washer
  objectType = a2pPart
  sourceFile = converted
  subassemblyImport = false
  timeLastImport = 1.689e+09
  updateColors = true
FEATURE [App::FeaturePython] circularEdge_028  label="circularEdge_028__F6951_006"  # a2plus constraint (typed FeaturePython)
  Object1 = b_M5_Arandela_001_004
  Object2 = b_F6951_001_005
  ParentTreeObject = -> b_M5_Arandela_001_004
  SubElement1 = Edge3
  SubElement2 = Edge13
  Suppressed = false
  Type = circularEdge
  directionConstraint = 1
  lockRotation = false
  offset = 0
FEATURE [App::FeaturePython] circularEdge_028_mirror  label="circularEdge_028__M5-Arandela_006"  # a2plus constraint (typed FeaturePython)
  Object1 = b_M5_Arandela_001_004
  Object2 = b_F6951_001_005
  ParentTreeObject = -> b_F6951_001_005
  SubElement1 = Edge3
  SubElement2 = Edge13
  Suppressed = false
  Type = circularEdge
  directionConstraint = 1
  lockRotation = false
  offset = 0
FEATURE [App::FeaturePython] circularEdge_029  label="circularEdge_029__F6951_011"  # a2plus constraint (typed FeaturePython)
  Object1 = b_M5_Arandela_001_003
  Object2 = b_F6951_001_010
  ParentTreeObject = -> b_M5_Arandela_001_003
  SubElement1 = Edge2
  SubElement2 = Edge14
  Suppressed = false
  Type = circularEdge
  directionConstraint = 1
  lockRotation = false
  offset = 0
FEATURE [App::FeaturePython] circularEdge_029_mirror  label="circularEdge_029__M5-Arandela_005"  # a2plus constraint (typed FeaturePython)
  Object1 = b_M5_Arandela_001_003
  Object2 = b_F6951_001_010
  ParentTreeObject = -> b_F6951_001_010
  SubElement1 = Edge2
  SubElement2 = Edge14
  Suppressed = false
  Type = circularEdge
  directionConstraint = 1
  lockRotation = false
  offset = 0
FEATURE [Part::FeaturePython] b__17_Elbow_001_  label="#17_Elbow_001"  # a2plus imported part (geometry in sourceFile) (typed FeaturePython)
  Placement = pos=(170,5.50212e-08,25) rot=(0,0,-1;1.48228rad)
  a2p_Version = 0.4.60k
  fixedPosition = false
  objectType = a2pPart
  sourceFile = .\#17_Elbow.FCStd
  subassemblyImport = false
  timeLastImport = 1.689e+09
  updateColors = true
FEATURE [Part::FeaturePython] b_M5_Arandela_001_005  label="M5-Arandela_007"  # a2plus imported part (geometry in sourceFile) (typed FeaturePython)
  Placement = pos=(170,-8.78369e-09,23) rot=(0.862017,0.50688,0;3.14159rad)
  a2p_Version = 0.4.60k
  fixedPosition = false
  localSourceObject = Washer
  objectType = a2pPart
  sourceFile = converted
  subassemblyImport = false
  timeLastImport = 1.689e+09
  updateColors = true
FEATURE [App::FeaturePython] circularEdge_030  label="circularEdge_030__F6951_003"  # a2plus constraint (typed FeaturePython)
  Object1 = b_M5_Arandela_001_005
  Object2 = b_F6951_001_002
  ParentTreeObject = -> b_M5_Arandela_001_005
  SubElement1 = Edge3
  SubElement2 = Edge8
  Suppressed = false
  Type = circularEdge
  directionConstraint = 0
  lockRotation = false
  offset = 0
FEATURE [App::FeaturePython] circularEdge_030_mirror  label="circularEdge_030__M5-Arandela_007"  # a2plus constraint (typed FeaturePython)
  Object1 = b_M5_Arandela_001_005
  Object2 = b_F6951_001_002
  ParentTreeObject = -> b_F6951_001_002
  SubElement1 = Edge3
  SubElement2 = Edge8
  Suppressed = false
  Type = circularEdge
  directionConstraint = 0
  lockRotation = false
  offset = 0
FEATURE [App::FeaturePython] circularEdge_031  label="circularEdge_031__M5-Arandela_007"  # a2plus constraint (typed FeaturePython)
  Object1 = b__17_Elbow_001_
  Object2 = b_M5_Arandela_001_005
  ParentTreeObject = -> b__17_Elbow_001_
  SubElement1 = Edge51
  SubElement2 = Edge1
  Suppressed = false
  Type = circularEdge
  directionConstraint = 0
  lockRotation = false
  offset = 0
FEATURE [App::FeaturePython] circularEdge_031_mirror  label="circularEdge_031__#17_Elbow_001"  # a2plus constraint (typed FeaturePython)
  Object1 = b__17_Elbow_001_
  Object2 = b_M5_Arandela_001_005
  ParentTreeObject = -> b_M5_Arandela_001_005
  SubElement1 = Edge51
  SubElement2 = Edge1
  Suppressed = false
  Type = circularEdge
  directionConstraint = 0
  lockRotation = false
  offset = 0
FEATURE [Part::FeaturePython] b_M5_Arandela_001_007  label="M5-Arandela_009"  # a2plus imported part (geometry in sourceFile) (typed FeaturePython)
  Placement = pos=(189.958,28.7519,34) rot=(0.876968,0.480548,0;3.14159rad)
  a2p_Version = 0.4.60k
  fixedPosition = false
  localSourceObject = Washer
  objectType = a2pPart
  sourceFile = converted
  subassemblyImport = false
  timeLastImport = 1.689e+09
  updateColors = true
FEATURE [App::FeaturePython] circularEdge_038  label="circularEdge_038__#17_Elbow_001"  # a2plus constraint (typed FeaturePython)
  Object1 = b_M5_Arandela_001_007
  Object2 = b__17_Elbow_001_
  ParentTreeObject = -> b_M5_Arandela_001_007
  SubElement1 = Edge3
  SubElement2 = Edge35
  Suppressed = false
  Type = circularEdge
  directionConstraint = 0
  lockRotation = false
  offset = 0
FEATURE [App::FeaturePython] circularEdge_038_mirror  label="circularEdge_038__M5-Arandela_009"  # a2plus constraint (typed FeaturePython)
  Object1 = b_M5_Arandela_001_007
  Object2 = b__17_Elbow_001_
  ParentTreeObject = -> b__17_Elbow_001_
  SubElement1 = Edge3
  SubElement2 = Edge35
  Suppressed = false
  Type = circularEdge
  directionConstraint = 0
  lockRotation = false
  offset = 0
FEATURE [Part::FeaturePython] b__15_Joint1Parallel_001_  label="#15_Joint1Parallel_001"  # a2plus imported part (geometry in sourceFile) (typed FeaturePython)
  Placement = pos=(14.5419,-31.8361,9) rot=(0.707107,0.707107,0;3.14159rad)
  a2p_Version = 0.4.60k
  fixedPosition = false
  objectType = a2pPart
  sourceFile = .\#15_Joint1Parallel.FCStd
  subassemblyImport = false
  timeLastImport = 1.6896e+09
  updateColors = true
FEATURE [App::FeaturePython] circularEdge_016  label="circularEdge_016__F6951_012"  # a2plus constraint (typed FeaturePython)
  Object1 = b__15_Joint1Parallel_001_
  Object2 = b_F6951_001_011
  ParentTreeObject = -> b__15_Joint1Parallel_001_
  SubElement1 = Edge45
  SubElement2 = Edge18
  Suppressed = false
  Type = circularEdge
  directionConstraint = 0
  lockRotation = false
  offset = 0
FEATURE [App::FeaturePython] circularEdge_016_mirror  label="circularEdge_016__#15_Joint1Parallel_001"  # a2plus constraint (typed FeaturePython)
  Object1 = b__15_Joint1Parallel_001_
  Object2 = b_F6951_001_011
  ParentTreeObject = -> b_F6951_001_011
  SubElement1 = Edge45
  SubElement2 = Edge18
  Suppressed = false
  Type = circularEdge
  directionConstraint = 0
  lockRotation = false
  offset = 0
FEATURE [App::FeaturePython] circularEdge_020_mirror  label="circularEdge_020__F6951_005"  # a2plus constraint (typed FeaturePython)
  Object1 = b_F6951_001_012
  Object2 = b__15_Joint1Parallel_001_
  ParentTreeObject = -> b__15_Joint1Parallel_001_
  SubElement1 = Edge18
  SubElement2 = Edge17
  Suppressed = false
  Type = circularEdge
  directionConstraint = 1
  lockRotation = false
  offset = 0
FEATURE [Part::FeaturePython] b_F6951_001_012  label="F6951_005"  # a2plus imported part (geometry in sourceFile) (typed FeaturePython)
  Placement = pos=(14.5419,-31.8361,6) rot=(0,0,-1;1.00916rad)
  a2p_Version = 0.4.60k
  fixedPosition = false
  objectType = a2pPart
  sourceFile = .\..\Complements\F695.step
  subassemblyImport = false
  timeLastImport = 1.6885e+09
  updateColors = true
FEATURE [App::FeaturePython] circularEdge_020  label="circularEdge_020__#15_Joint1Parallel_001"  # a2plus constraint (typed FeaturePython)
  Object1 = b_F6951_001_012
  Object2 = b__15_Joint1Parallel_001_
  ParentTreeObject = -> b_F6951_001_012
  SubElement1 = Edge18
  SubElement2 = Edge17
  Suppressed = false
  Type = circularEdge
  directionConstraint = 1
  lockRotation = false
  offset = 0
FEATURE [Part::FeaturePython] b_M5_Arandela_001_008  label="M5-Arandela_008"  # a2plus imported part (geometry in sourceFile) (typed FeaturePython)
  Placement = pos=(195.171,-31.0872,45) rot=(0.841392,0.540425,-1e-06;3.14159rad)
  a2p_Version = 0.4.60k
  fixedPosition = false
  localSourceObject = Washer
  objectType = a2pPart
  sourceFile = converted
  subassemblyImport = false
  timeLastImport = 1.689e+09
  updateColors = true
FEATURE [Part::FeaturePython] b_F6951_001_013  label="F6951_013"  # a2plus imported part (geometry in sourceFile) (typed FeaturePython)
  Placement = pos=(195.171,-31.0872,51) rot=(0.71339,-0.700767,-2e-06;3.14159rad)
  a2p_Version = 0.4.60k
  fixedPosition = false
  objectType = a2pPart
  sourceFile = .\..\Complements\F695.step
  subassemblyImport = false
  timeLastImport = 1.6885e+09
  updateColors = true
FEATURE [Part::FeaturePython] b__20_Link2Parallel_001_  label="#20_Link2Parallel_001"  # a2plus imported part (geometry in sourceFile) (typed FeaturePython)
  Placement = pos=(189.958,28.7519,47) rot=(0.54061,0.841273,0;3.14159rad)
  a2p_Version = 0.4.60k
  fixedPosition = false
  objectType = a2pPart
  sourceFile = .\#20_Link2Parallel.FCStd
  subassemblyImport = false
  timeLastImport = 1.68302e+09
  updateColors = true
FEATURE [Part::FeaturePython] b__16_EndEffectorParallel_001_  label="#16_EndEffectorParallel_001"  # a2plus imported part (geometry in sourceFile) (typed FeaturePython)
  Placement = pos=(25.1712,-31.0872,48.0008) rot=(-2e-06,2e-06,-1;1.5708rad)
  a2p_Version = 0.4.60k
  fixedPosition = false
  objectType = a2pPart
  sourceFile = .\#16_EndEffectorParallel.FCStd
  subassemblyImport = false
  timeLastImport = 1.68302e+09
  updateColors = true
FEATURE [App::FeaturePython] planesParallel_001  label="planesParallel_001__#11_Link1_001"  # a2plus constraint (typed FeaturePython)
  Object1 = b__16_EndEffectorParallel_001_
  Object2 = b__11_Link1_001_
  ParentTreeObject = -> b__16_EndEffectorParallel_001_
  SubElement1 = Face2
  SubElement2 = Face45
  Suppressed = false
  Type = planesParallel
  directionConstraint = 0
FEATURE [App::FeaturePython] planesParallel_001_mirror  label="planesParallel_001__#16_EndEffectorParallel_001"  # a2plus constraint (typed FeaturePython)
  Object1 = b__16_EndEffectorParallel_001_
  Object2 = b__11_Link1_001_
  ParentTreeObject = -> b__11_Link1_001_
  SubElement1 = Face2
  SubElement2 = Face45
  Suppressed = false
  Type = planesParallel
  directionConstraint = 0
FEATURE [Part::FeaturePython] b_F6951_001_014  label="F6951_014"  # a2plus imported part (geometry in sourceFile) (typed FeaturePython)
  Placement = pos=(25.1712,-31.0872,51.0008) rot=(0.71339,-0.700767,-2e-06;3.14159rad)
  a2p_Version = 0.4.60k
  fixedPosition = false
  objectType = a2pPart
  sourceFile = .\..\Complements\F695.step
  subassemblyImport = false
  timeLastImport = 1.6885e+09
  updateColors = true
FEATURE [App::FeaturePython] circularEdge_035  label="circularEdge_035__#16_EndEffectorParallel_001"  # a2plus constraint (typed FeaturePython)
  Object1 = b_F6951_001_014
  Object2 = b__16_EndEffectorParallel_001_
  ParentTreeObject = -> b_F6951_001_014
  SubElement1 = Edge18
  SubElement2 = Edge12
  Suppressed = false
  Type = circularEdge
  directionConstraint = 1
  lockRotation = false
  offset = 0
FEATURE [App::FeaturePython] circularEdge_035_mirror  label="circularEdge_035__F6951_014"  # a2plus constraint (typed FeaturePython)
  Object1 = b_F6951_001_014
  Object2 = b__16_EndEffectorParallel_001_
  ParentTreeObject = -> b__16_EndEffectorParallel_001_
  SubElement1 = Edge18
  SubElement2 = Edge12
  Suppressed = false
  Type = circularEdge
  directionConstraint = 1
  lockRotation = false
  offset = 0
FEATURE [Part::FeaturePython] b_M5_Arandela_001_009  label="M5-Arandela_010"  # a2plus imported part (geometry in sourceFile) (typed FeaturePython)
  Placement = pos=(195.171,-31.0872,44.9999) rot=(0.841392,0.540425,-2e-06;3.14159rad)
  a2p_Version = 0.4.60k
  fixedPosition = false
  localSourceObject = Washer
  objectType = a2pPart
  sourceFile = converted
  subassemblyImport = false
  timeLastImport = 1.689e+09
  updateColors = true
FEATURE [Part::FeaturePython] b_M5_Arandela_001_010  label="M5-Arandela_011"  # a2plus imported part (geometry in sourceFile) (typed FeaturePython)
  Placement = pos=(25.1712,-31.0872,45.0008) rot=(0.841392,0.540425,-2e-06;3.1416rad)
  a2p_Version = 0.4.60k
  fixedPosition = false
  localSourceObject = Washer
  objectType = a2pPart
  sourceFile = converted
  subassemblyImport = false
  timeLastImport = 1.689e+09
  updateColors = true
FEATURE [App::FeaturePython] circularEdge_036  label="circularEdge_036__F6951_014"  # a2plus constraint (typed FeaturePython)
  Object1 = b_M5_Arandela_001_010
  Object2 = b_F6951_001_014
  ParentTreeObject = -> b_M5_Arandela_001_010
  SubElement1 = Edge2
  SubElement2 = Edge14
  Suppressed = false
  Type = circularEdge
  directionConstraint = 1
  lockRotation = false
  offset = 0
FEATURE [App::FeaturePython] circularEdge_036_mirror  label="circularEdge_036__M5-Arandela_011"  # a2plus constraint (typed FeaturePython)
  Object1 = b_M5_Arandela_001_010
  Object2 = b_F6951_001_014
  ParentTreeObject = -> b_F6951_001_014
  SubElement1 = Edge2
  SubElement2 = Edge14
  Suppressed = false
  Type = circularEdge
  directionConstraint = 1
  lockRotation = false
  offset = 0
FEATURE [Part::FeaturePython] b_F6951_001_015  label="F6951_015"  # a2plus imported part (geometry in sourceFile) (typed FeaturePython)
  Placement = pos=(195.171,-31.0872,55) rot=(-2e-06,6e-06,-1;0.771534rad)
  a2p_Version = 0.4.60k
  fixedPosition = false
  objectType = a2pPart
  sourceFile = .\..\Complements\F695.step
  subassemblyImport = false
  timeLastImport = 1.6885e+09
  updateColors = true
FEATURE [App::FeaturePython] circularEdge_037  label="circularEdge_037__#16_EndEffectorParallel_001"  # a2plus constraint (typed FeaturePython)
  Object1 = b_F6951_001_015
  Object2 = b__16_EndEffectorParallel_001_
  ParentTreeObject = -> b_F6951_001_015
  SubElement1 = Edge18
  SubElement2 = Edge56
  Suppressed = false
  Type = circularEdge
  directionConstraint = 0
  lockRotation = false
  offset = 0
FEATURE [App::FeaturePython] circularEdge_037_mirror  label="circularEdge_037__F6951_015"  # a2plus constraint (typed FeaturePython)
  Object1 = b_F6951_001_015
  Object2 = b__16_EndEffectorParallel_001_
  ParentTreeObject = -> b__16_EndEffectorParallel_001_
  SubElement1 = Edge18
  SubElement2 = Edge56
  Suppressed = false
  Type = circularEdge
  directionConstraint = 0
  lockRotation = false
  offset = 0
FEATURE [Part::FeaturePython] b_F6951_001_016  label="F6951_016"  # a2plus imported part (geometry in sourceFile) (typed FeaturePython)
  Placement = pos=(25.1713,-31.0872,55.0008) rot=(-2e-06,6e-06,-1;0.771534rad)
  a2p_Version = 0.4.60k
  fixedPosition = false
  objectType = a2pPart
  sourceFile = .\..\Complements\F695.step
  subassemblyImport = false
  timeLastImport = 1.6885e+09
  updateColors = true
FEATURE [App::FeaturePython] circularEdge_039  label="circularEdge_039__#16_EndEffectorParallel_001"  # a2plus constraint (typed FeaturePython)
  Object1 = b_F6951_001_016
  Object2 = b__16_EndEffectorParallel_001_
  ParentTreeObject = -> b_F6951_001_016
  SubElement1 = Edge18
  SubElement2 = Edge43
  Suppressed = false
  Type = circularEdge
  directionConstraint = 0
  lockRotation = false
  offset = 0
FEATURE [App::FeaturePython] circularEdge_039_mirror  label="circularEdge_039__F6951_016"  # a2plus constraint (typed FeaturePython)
  Object1 = b_F6951_001_016
  Object2 = b__16_EndEffectorParallel_001_
  ParentTreeObject = -> b__16_EndEffectorParallel_001_
  SubElement1 = Edge18
  SubElement2 = Edge43
  Suppressed = false
  Type = circularEdge
  directionConstraint = 0
  lockRotation = false
  offset = 0
FEATURE [Part::FeaturePython] b_F6951_001_017  label="F6951_017"  # a2plus imported part (geometry in sourceFile) (typed FeaturePython)
  Placement = pos=(189.958,28.7519,40) rot=(0.967165,-0.25415,0;3.14159rad)
  a2p_Version = 0.4.60k
  fixedPosition = false
  objectType = a2pPart
  sourceFile = .\..\Complements\F695.step
  subassemblyImport = false
  timeLastImport = 1.6885e+09
  updateColors = true
FEATURE [Part::FeaturePython] b_F6951_001_018  label="F6951_018"  # a2plus imported part (geometry in sourceFile) (typed FeaturePython)
  Placement = pos=(189.958,28.7519,44) rot=(-1e-06,0,-1;0.77153rad)
  a2p_Version = 0.4.60k
  fixedPosition = false
  objectType = a2pPart
  sourceFile = .\..\Complements\F695.step
  subassemblyImport = false
  timeLastImport = 1.6885e+09
  updateColors = true
FEATURE [App::FeaturePython] circularEdge_041  label="circularEdge_041__M5-Arandela_009"  # a2plus constraint (typed FeaturePython)
  Object1 = b_F6951_001_017
  Object2 = b_M5_Arandela_001_007
  ParentTreeObject = -> b_F6951_001_017
  SubElement1 = Edge14
  SubElement2 = Edge2
  Suppressed = false
  Type = circularEdge
  directionConstraint = 1
  lockRotation = false
  offset = 0
FEATURE [App::FeaturePython] circularEdge_041_mirror  label="circularEdge_041__F6951_017"  # a2plus constraint (typed FeaturePython)
  Object1 = b_F6951_001_017
  Object2 = b_M5_Arandela_001_007
  ParentTreeObject = -> b_M5_Arandela_001_007
  SubElement1 = Edge14
  SubElement2 = Edge2
  Suppressed = false
  Type = circularEdge
  directionConstraint = 1
  lockRotation = false
  offset = 0
FEATURE [App::FeaturePython] circularEdge_040  label="circularEdge_040__F6951_017"  # a2plus constraint (typed FeaturePython)
  Object1 = b__20_Link2Parallel_001_
  Object2 = b_F6951_001_017
  ParentTreeObject = -> b__20_Link2Parallel_001_
  SubElement1 = Edge55
  SubElement2 = Edge18
  Suppressed = false
  Type = circularEdge
  directionConstraint = 0
  lockRotation = false
  offset = 0
FEATURE [App::FeaturePython] circularEdge_040_mirror  label="circularEdge_040__#20_Link2Parallel_001"  # a2plus constraint (typed FeaturePython)
  Object1 = b__20_Link2Parallel_001_
  Object2 = b_F6951_001_017
  ParentTreeObject = -> b_F6951_001_017
  SubElement1 = Edge55
  SubElement2 = Edge18
  Suppressed = false
  Type = circularEdge
  directionConstraint = 0
  lockRotation = false
  offset = 0
FEATURE [App::FeaturePython] circularEdge_042  label="circularEdge_042__#20_Link2Parallel_001"  # a2plus constraint (typed FeaturePython)
  Object1 = b_F6951_001_018
  Object2 = b__20_Link2Parallel_001_
  ParentTreeObject = -> b_F6951_001_018
  SubElement1 = Edge18
  SubElement2 = Edge18
  Suppressed = false
  Type = circularEdge
  directionConstraint = 1
  lockRotation = false
  offset = 0
FEATURE [App::FeaturePython] circularEdge_042_mirror  label="circularEdge_042__F6951_018"  # a2plus constraint (typed FeaturePython)
  Object1 = b_F6951_001_018
  Object2 = b__20_Link2Parallel_001_
  ParentTreeObject = -> b__20_Link2Parallel_001_
  SubElement1 = Edge18
  SubElement2 = Edge18
  Suppressed = false
  Type = circularEdge
  directionConstraint = 1
  lockRotation = false
  offset = 0
FEATURE [Part::FeaturePython] Screw016  label="M5x40-Tornillo"  # Fasteners workbench fastener (typed FeaturePython)
  Placement = pos=(195.171,-31.0872,59) rot=(-0.001902,0.999998,0;5e-06rad)
  baseObject = -> b_F6951_001_015 [Edge8]
  diameter = 6
  invert = false
  leftHanded = false
  length = 12
  lengthCustom = 40
  matchOuter = false
  offset = 0
  thread = false
  type = 45
FEATURE [Part::FeaturePython] Nut015  label="M5-Tuerca001"  # Fasteners workbench fastener (typed FeaturePython)
  Placement = pos=(195.171,-31.0872,25) rot=(0.056391,0.998409,0;3.14159rad)
  baseObject = -> b__17_Elbow_001_ [Edge52]
  diameter = 3
  invert = true
  leftHanded = false
  matchOuter = false
  offset = 0
  thread = false
  type = 19
FEATURE [Part::FeaturePython] Nut016  label="M5-Tuerca002"  # Fasteners workbench fastener (typed FeaturePython)
  Placement = pos=(170,-4.2352e-06,35) rot=(0.056391,0.998409,0;2e-06rad)
  baseObject = -> b__17_Elbow_001_ [Edge22]
  diameter = 3
  invert = false
  leftHanded = false
  matchOuter = false
  offset = 0
  thread = false
  type = 19
FEATURE [Part::FeaturePython] Screw017  label="M5x60-Tornillo"  # Fasteners workbench fastener (typed FeaturePython)
  Placement = pos=(170,5.62755e-06,-19) rot=(0.827545,0.561399,0;3.14159rad)
  baseObject = -> b_F6951_001_007 [Edge17]
  diameter = 6
  invert = true
  leftHanded = false
  length = 12
  lengthCustom = 60
  matchOuter = false
  offset = 0
  thread = false
  type = 45
FEATURE [Part::FeaturePython] Screw019  label="M5x30-Tornillo"  # Fasteners workbench fastener (typed FeaturePython)
  Placement = pos=(190.042,28.6932,48) rot=(0.52846,0.848958,0;2e-06rad)
  baseObject = -> b_F6951_001_018 [Edge17]
  diameter = 6
  invert = true
  leftHanded = false
  length = 12
  lengthCustom = 30
  matchOuter = false
  offset = 0
  thread = false
  type = 45
FEATURE [Part::FeaturePython] Nut018  label="M5-Tuerca004"  # Fasteners workbench fastener (typed FeaturePython)
  Placement = pos=(190.042,28.6932,25) rot=(0.056391,0.998409,0;3.14159rad)
  baseObject = -> b__17_Elbow_001_ [Edge47]
  diameter = 3
  invert = true
  leftHanded = false
  matchOuter = false
  offset = 0
  thread = false
  type = 19
FEATURE [App::FeaturePython] circularEdge_021  label="circularEdge_021__#15_Joint1Parallel_001"  # a2plus constraint (typed FeaturePython)
  Object1 = b_M5_Arandela_001_001
  Object2 = b__15_Joint1Parallel_001_
  ParentTreeObject = -> b_M5_Arandela_001_001
  SubElement1 = Edge2
  SubElement2 = Edge40
  Suppressed = false
  Type = circularEdge
  directionConstraint = 1
  lockRotation = false
  offset = 0
FEATURE [App::FeaturePython] circularEdge_021_mirror  label="circularEdge_021__M5-Arandela_003"  # a2plus constraint (typed FeaturePython)
  Object1 = b_M5_Arandela_001_001
  Object2 = b__15_Joint1Parallel_001_
  ParentTreeObject = -> b__15_Joint1Parallel_001_
  SubElement1 = Edge2
  SubElement2 = Edge40
  Suppressed = false
  Type = circularEdge
  directionConstraint = 1
  lockRotation = false
  offset = 0
FEATURE [Part::FeaturePython] Screw015  label="M5x25-Tornillo"  # Fasteners workbench fastener (typed FeaturePython)
  Placement = pos=(14.5419,-31.8361,10) rot=(0.77032,0.637658,0;1e-06rad)
  baseObject = -> b_F6951_001_012 [Edge8]
  diameter = 6
  invert = false
  leftHanded = false
  length = 12
  lengthCustom = 25
  matchOuter = false
  offset = 0
  thread = false
  type = 45
FEATURE [Part::FeaturePython] Nut019  label="M5-Tuerca"  # Fasteners workbench fastener (typed FeaturePython)
  Placement = pos=(14.5419,-31.8361,-11) rot=(0.800746,0.599004,0;3.14159rad)
  baseObject = -> b__14_Joint2Crank_001_ [Edge69]
  diameter = 3
  invert = false
  leftHanded = false
  matchOuter = false
  offset = 0
  thread = false
  type = 19
FEATURE [App::FeaturePython] planesParallel_002  label="planesParallel_002__#19_Link2_001"  # a2plus constraint (typed FeaturePython)
  Object1 = b__20_Link2Parallel_001_
  Object2 = b__19_Link2_001_
  ParentTreeObject = -> b__20_Link2Parallel_001_
  SubElement1 = Face11
  SubElement2 = Face2
  Suppressed = false
  Type = planesParallel
  directionConstraint = 1
FEATURE [App::FeaturePython] planesParallel_002_mirror  label="planesParallel_002__#20_Link2Parallel_001"  # a2plus constraint (typed FeaturePython)
  Object1 = b__20_Link2Parallel_001_
  Object2 = b__19_Link2_001_
  ParentTreeObject = -> b__19_Link2_001_
  SubElement1 = Face11
  SubElement2 = Face2
  Suppressed = false
  Type = planesParallel
  directionConstraint = 1
FEATURE [Part::FeaturePython] Screw020  label="M5x30-Tornillo001"  # Fasteners workbench fastener (typed FeaturePython)
  Placement = pos=(184.542,-31.836,-19) rot=(0.827642,0.561256,0;3.14159rad)
  baseObject = -> b_F6951_001_009 [Edge17]
  diameter = 6
  invert = true
  leftHanded = false
  length = 12
  lengthCustom = 30
  matchOuter = false
  offset = 0
  thread = false
  type = 45
FEATURE [Part::FeaturePython] Nut020  label="M6-Tuerca"  # Fasteners workbench fastener (typed FeaturePython)
  Placement = pos=(184.542,-31.8361,8.99999) rot=(0.938763,0.344563,0;3.14159rad)
  baseObject = -> b__15_Joint1Parallel_001_ [Edge30]
  diameter = 4
  invert = false
  leftHanded = false
  matchOuter = false
  offset = 0
  thread = false
  type = 19
FEATURE [Part::FeaturePython] Nut017  label="M5-Tuerca005"  # Fasteners workbench fastener (typed FeaturePython)
  Placement = pos=(184.542,-31.8361,8.99999) rot=(0.938763,0.344563,0;0rad)
  baseObject = -> b__15_Joint1Parallel_001_ [Edge30]
  diameter = 3
  invert = true
  leftHanded = false
  matchOuter = false
  offset = 0
  thread = false
  type = 19
FEATURE [Part::FeaturePython] Screw021  label="M3x25-Tornillo"  # Fasteners workbench fastener (typed FeaturePython)
  Placement = pos=(-12.7599,-17.9216,-6) rot=(-0.106932,-0.994266,0;0rad)
  baseObject = -> b__14_Joint2Crank_001_ [Edge36]
  diameter = 4
  invert = false
  leftHanded = false
  length = 10
  lengthCustom = 25
  matchOuter = false
  offset = 0
  thread = false
  type = 45
FEATURE [Part::FeaturePython] Screw022  label="M3x25-Tornillo001"  # Fasteners workbench fastener (typed FeaturePython)
  Placement = pos=(9.14059,-20.0112,-6) rot=(-0.106932,-0.994266,0;0rad)
  baseObject = -> b__14_Joint2Crank_001_ [Edge55]
  diameter = 4
  invert = false
  leftHanded = false
  length = 10
  lengthCustom = 25
  matchOuter = false
  offset = 0
  thread = false
  type = 45
FEATURE [Part::FeaturePython] Screw023  label="M3x25-Tornillo002"  # Fasteners workbench fastener (typed FeaturePython)
  Placement = pos=(-21.9005,2.08963,-6) rot=(-0.106932,-0.994266,0;0rad)
  baseObject = -> b__14_Joint2Crank_001_ [Edge34]
  diameter = 4
  invert = false
  leftHanded = false
  length = 10
  lengthCustom = 25
  matchOuter = false
  offset = 0
  thread = false
  type = 45
FEATURE [Part::FeaturePython] Screw024  label="M3x25-Tornillo003"  # Fasteners workbench fastener (typed FeaturePython)
  Placement = pos=(-9.14059,20.0112,-6) rot=(-0.106932,-0.994266,0;0rad)
  baseObject = -> b__14_Joint2Crank_001_ [Edge50]
  diameter = 4
  invert = false
  leftHanded = false
  length = 10
  lengthCustom = 25
  matchOuter = false
  offset = 0
  thread = false
  type = 45
FEATURE [Part::FeaturePython] Screw025  label="M3x25-Tornillo004"  # Fasteners workbench fastener (typed FeaturePython)
  Placement = pos=(12.7599,17.9216,-6) rot=(-0.106932,-0.994266,0;0rad)
  baseObject = -> b__14_Joint2Crank_001_ [Edge53]
  diameter = 4
  invert = false
  leftHanded = false
  length = 10
  lengthCustom = 25
  matchOuter = false
  offset = 0
  thread = false
  type = 45
FEATURE [Part::FeaturePython] Screw026  label="M3x25-Tornillo005"  # Fasteners workbench fastener (typed FeaturePython)
  Placement = pos=(21.9005,-2.08963,-6) rot=(-0.106932,-0.994266,0;0rad)
  baseObject = -> b__14_Joint2Crank_001_ [Edge57]
  diameter = 4
  invert = false
  leftHanded = false
  length = 10
  lengthCustom = 25
  matchOuter = false
  offset = 0
  thread = false
  type = 45
FEATURE [Part::FeaturePython] Nut021  label="M3-Tuerca016"  # Fasteners workbench fastener (typed FeaturePython)
  Placement = pos=(-12.7599,-17.9216,-27) rot=(0.944639,0.328111,0;3.14159rad)
  baseObject = -> b__10_MotorsBasePulleys_001_001 [Edge2222]
  diameter = 1
  invert = false
  leftHanded = false
  matchOuter = false
  offset = 0
  thread = false
  type = 19
FEATURE [Part::FeaturePython] Nut022  label="M3-Tuerca017"  # Fasteners workbench fastener (typed FeaturePython)
  Placement = pos=(-21.9005,2.08963,-27) rot=(0.944639,0.328111,0;3.14159rad)
  baseObject = -> b__10_MotorsBasePulleys_001_001 [Edge2221]
  diameter = 1
  invert = false
  leftHanded = false
  matchOuter = false
  offset = 0
  thread = false
  type = 19
FEATURE [Part::FeaturePython] Nut023  label="M3-Tuerca018"  # Fasteners workbench fastener (typed FeaturePython)
  Placement = pos=(12.7599,17.9216,-27) rot=(0.944639,0.328111,0;3.14159rad)
  baseObject = -> b__10_MotorsBasePulleys_001_001 [Edge2225]
  diameter = 1
  invert = false
  leftHanded = false
  matchOuter = false
  offset = 0
  thread = false
  type = 19
FEATURE [Part::FeaturePython] Nut024  label="M3-Tuerca019"  # Fasteners workbench fastener (typed FeaturePython)
  Placement = pos=(21.9005,-2.08963,-27) rot=(0.944639,0.328111,0;3.14159rad)
  baseObject = -> b__10_MotorsBasePulleys_001_001 [Edge2226]
  diameter = 1
  invert = false
  leftHanded = false
  matchOuter = false
  offset = 0
  thread = false
  type = 19
FEATURE [Part::FeaturePython] Nut025  label="M3-Tuerca020"  # Fasteners workbench fastener (typed FeaturePython)
  Placement = pos=(9.1406,-20.0112,-27) rot=(0.944639,0.328111,0;3.14159rad)
  baseObject = -> b__10_MotorsBasePulleys_001_001 [Edge2224]
  diameter = 1
  invert = false
  leftHanded = false
  matchOuter = false
  offset = 0
  thread = false
  type = 19
FEATURE [Part::FeaturePython] Nut026  label="M3-Tuerca021"  # Fasteners workbench fastener (typed FeaturePython)
  Placement = pos=(-9.14059,20.0112,-27) rot=(0.944639,0.328111,0;3.14159rad)
  baseObject = -> b__10_MotorsBasePulleys_001_001 [Edge2223]
  diameter = 1
  invert = false
  leftHanded = false
  matchOuter = false
  offset = 0
  thread = false
  type = 19
FEATURE [Part::FeaturePython] Washer001  label="M3-Arandela"  # Fasteners workbench fastener (typed FeaturePython)
  Placement = pos=(92.9059,-35.3361,-1.00001) rot=(-0.938763,-0.344563,0;3.14159rad)
  baseObject = -> b__15_Joint1Parallel_001_ [Edge79]
  diameter = 4
  invert = false
  matchOuter = false
  offset = 0
  type = 4
FEATURE [Part::FeaturePython] Washer002  label="M3-Arandela001"  # Fasteners workbench fastener (typed FeaturePython)
  Placement = pos=(73.9059,-35.3361,-1) rot=(-0.938763,-0.344563,0;3.14159rad)
  baseObject = -> b__15_Joint1Parallel_001_ [Edge78]
  diameter = 4
  invert = false
  matchOuter = false
  offset = 0
  type = 4
FEATURE [Part::FeaturePython] Washer003  label="M3-Arandela002"  # Fasteners workbench fastener (typed FeaturePython)
  Placement = pos=(92.9059,-35.3361,-1.50001) rot=(-0.938763,-0.344563,0;3.14159rad)
  baseObject = -> Washer001 [Edge2]
  diameter = 4
  invert = false
  matchOuter = false
  offset = 0
  type = 4
FEATURE [Part::FeaturePython] Washer004  label="M3-Arandela003"  # Fasteners workbench fastener (typed FeaturePython)
  Placement = pos=(73.9059,-35.3361,-1.5) rot=(-0.938763,-0.344563,0;3.14159rad)
  baseObject = -> Washer002 [Edge2]
  diameter = 4
  invert = false
  matchOuter = false
  offset = 0
  type = 4
FEATURE [Part::FeaturePython] Washer005  label="M3-Arandela004"  # Fasteners workbench fastener (typed FeaturePython)
  Placement = pos=(92.9059,-35.3361,-1.50001) rot=(-0.938763,-0.344563,0;3.14159rad)
  baseObject = -> Washer001 [Edge2]
  diameter = 4
  invert = false
  matchOuter = false
  offset = 0
  type = 4
FEATURE [Part::FeaturePython] Washer006  label="M3-Arandela005"  # Fasteners workbench fastener (typed FeaturePython)
  Placement = pos=(73.9059,-35.3361,-1.5) rot=(-0.938763,-0.344563,0;3.14159rad)
  baseObject = -> Washer002 [Edge2]
  diameter = 4
  invert = false
  matchOuter = false
  offset = 0
  type = 4
FEATURE [Part::FeaturePython] Washer007  label="M3-Arandela006"  # Fasteners workbench fastener (typed FeaturePython)
  Placement = pos=(92.9059,-35.3361,-2.00001) rot=(-0.938763,-0.344563,0;3.14159rad)
  baseObject = -> Washer003 [Edge2]
  diameter = 4
  invert = false
  matchOuter = false
  offset = 0
  type = 4
FEATURE [Part::FeaturePython] Washer008  label="M3-Arandela007"  # Fasteners workbench fastener (typed FeaturePython)
  Placement = pos=(73.9059,-35.3361,-2) rot=(-0.938763,-0.344563,0;3.14159rad)
  baseObject = -> Washer004 [Edge2]
  diameter = 4
  invert = false
  matchOuter = false
  offset = 0
  type = 4
FEATURE [Part::FeaturePython] Washer009  label="M3-Arandela008"  # Fasteners workbench fastener (typed FeaturePython)
  Placement = pos=(92.9059,-35.3361,-1.50001) rot=(-0.938763,-0.344563,0;3.14159rad)
  baseObject = -> Washer001 [Edge2]
  diameter = 4
  invert = false
  matchOuter = false
  offset = 0
  type = 4
FEATURE [Part::FeaturePython] Washer010  label="M3-Arandela009"  # Fasteners workbench fastener (typed FeaturePython)
  Placement = pos=(73.9059,-35.3361,-1.5) rot=(-0.938763,-0.344563,0;3.14159rad)
  baseObject = -> Washer002 [Edge2]
  diameter = 4
  invert = false
  matchOuter = false
  offset = 0
  type = 4
FEATURE [Part::FeaturePython] Washer011  label="M3-Arandela010"  # Fasteners workbench fastener (typed FeaturePython)
  Placement = pos=(92.9059,-35.3361,-2.00001) rot=(-0.938763,-0.344563,0;3.14159rad)
  baseObject = -> Washer003 [Edge2]
  diameter = 4
  invert = false
  matchOuter = false
  offset = 0
  type = 4
FEATURE [Part::FeaturePython] Washer012  label="M3-Arandela011"  # Fasteners workbench fastener (typed FeaturePython)
  Placement = pos=(73.9059,-35.3361,-2) rot=(-0.938763,-0.344563,0;3.14159rad)
  baseObject = -> Washer004 [Edge2]
  diameter = 4
  invert = false
  matchOuter = false
  offset = 0
  type = 4
FEATURE [Part::FeaturePython] Washer013  label="M3-Arandela012"  # Fasteners workbench fastener (typed FeaturePython)
  Placement = pos=(92.9059,-35.3361,-2.50001) rot=(-0.938763,-0.344563,0;3.14159rad)
  baseObject = -> Washer007 [Edge2]
  diameter = 4
  invert = false
  matchOuter = false
  offset = 0
  type = 4
FEATURE [Part::FeaturePython] Washer014  label="M3-Arandela013"  # Fasteners workbench fastener (typed FeaturePython)
  Placement = pos=(73.9059,-35.3361,-2.5) rot=(-0.938763,-0.344563,0;3.14159rad)
  baseObject = -> Washer008 [Edge2]
  diameter = 4
  invert = false
  matchOuter = false
  offset = 0
  type = 4
FEATURE [Part::FeaturePython] b_Endstop1_001_  label="Endstop1_001"  # a2plus imported part (geometry in sourceFile) (typed FeaturePython)
  Placement = pos=(89.2054,-40.2981,-2.98504) rot=(0,0,1;0rad)
  a2p_Version = 0.4.60k
  fixedPosition = false
  objectType = a2pPart
  sourceFile = .\..\Complements\Endstop.step
  subassemblyImport = false
  timeLastImport = 1.68866e+09
  updateColors = true
FEATURE [App::FeaturePython] axisCoincident_001  label="axisCoincident_001__#15_Joint1Parallel_001"  # a2plus constraint (typed FeaturePython)
  Object1 = b_Endstop1_001_
  Object2 = b__15_Joint1Parallel_001_
  ParentTreeObject = -> b_Endstop1_001_
  SubElement1 = Edge67
  SubElement2 = Edge78
  Suppressed = false
  Type = axial
  directionConstraint = 0
  lockRotation = false
FEATURE [App::FeaturePython] axisCoincident_001_mirror  label="axisCoincident_001__Endstop1_001"  # a2plus constraint (typed FeaturePython)
  Object1 = b_Endstop1_001_
  Object2 = b__15_Joint1Parallel_001_
  ParentTreeObject = -> b__15_Joint1Parallel_001_
  SubElement1 = Edge67
  SubElement2 = Edge78
  Suppressed = false
  Type = axial
  directionConstraint = 0
  lockRotation = false
FEATURE [Part::FeaturePython] Screw027  label="M3x12-Tornillo"  # Fasteners workbench fastener (typed FeaturePython)
  Placement = pos=(92.9554,-35.2981,-3.98504) rot=(-1,0,0;3.14159rad)
  baseObject = -> b_Endstop1_001_ [Edge58]
  diameter = 3
  invert = true
  leftHanded = false
  length = 9
  lengthCustom = 12
  matchOuter = false
  offset = 0
  thread = false
  type = 31
FEATURE [Part::FeaturePython] Screw028  label="M3x12-Tornillo001"  # Fasteners workbench fastener (typed FeaturePython)
  Placement = pos=(73.9554,-35.2981,-3.98504) rot=(-1,0,0;3.14159rad)
  baseObject = -> b_Endstop1_001_ [Edge59]
  diameter = 3
  invert = true
  leftHanded = false
  length = 9
  lengthCustom = 12
  matchOuter = false
  offset = 0
  thread = false
  type = 31
FEATURE [Part::FeaturePython] Nut027  label="M3-Tuerca022"  # Fasteners workbench fastener (typed FeaturePython)
  Placement = pos=(92.9059,-35.3361,3.99999) rot=(0.938763,0.344563,0;0rad)
  baseObject = -> b__15_Joint1Parallel_001_ [Edge143]
  diameter = 1
  invert = false
  leftHanded = false
  matchOuter = false
  offset = 0
  thread = false
  type = 19
FEATURE [Part::FeaturePython] Nut028  label="M3-Tuerca023"  # Fasteners workbench fastener (typed FeaturePython)
  Placement = pos=(73.9059,-35.3361,4) rot=(0.938763,0.344563,0;0rad)
  baseObject = -> b__15_Joint1Parallel_001_ [Edge141]
  diameter = 1
  invert = false
  leftHanded = false
  matchOuter = false
  offset = 0
  thread = false
  type = 19
